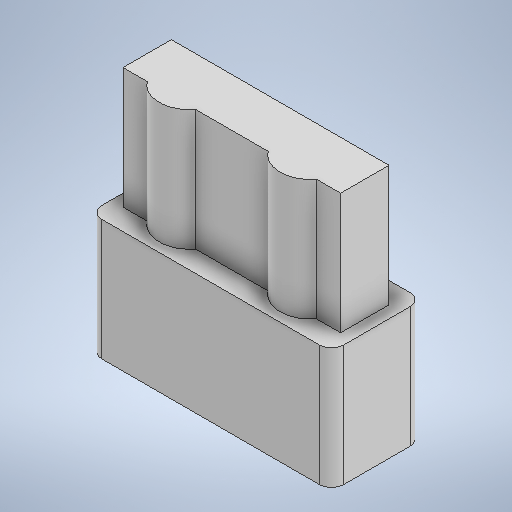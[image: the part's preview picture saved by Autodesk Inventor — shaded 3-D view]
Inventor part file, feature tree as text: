
AUTODESK INVENTOR PART (.ipt)
format: ipt  version: 2025.2 (Build 292293000, 293)  size: 241,664 bytes
history: native  units: mm
features: extrude x2, sketch x2, other x1, fillet x1
ambient origin geometry x8: Origin, YZ Plane, XZ Plane, XY Plane, X Axis, Y Axis, Z Axis, Center Point
bodies: Body1 (feature_tree)
feature tree (6):
  other  "Bryła1"
  extrude  "Wyciągnięcie proste1"  Depth=40.0mm
  extrude  "Wyciągnięcie proste2"  Depth=15.0mm
  fillet  "Zaokrąglenie1"  Radius=20.0mm
  sketch  "Szkic2"
  sketch  "Szkic3"
